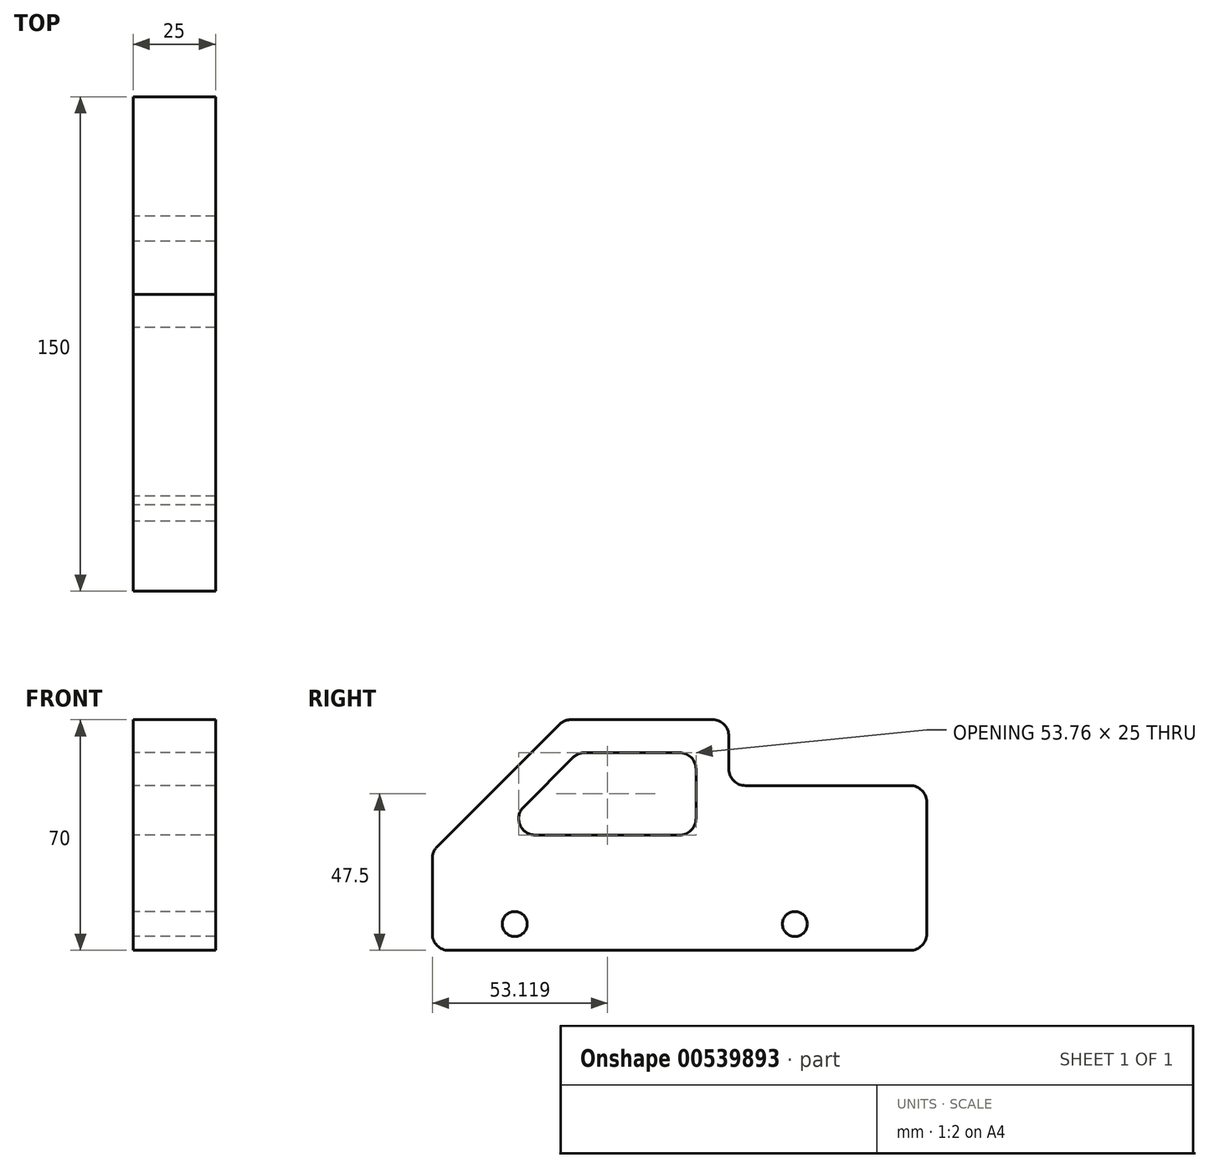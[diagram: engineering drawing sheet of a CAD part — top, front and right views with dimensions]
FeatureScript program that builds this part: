
annotation { "Feature Type Name" : "Feature", "Feature Type Description" : "" }
export const myFeature = defineFeature(function(context is Context, id is Id, definition is map)
    precondition{}
    {
        {
            var Q0;
            Q0=qCreatedBy(makeId("Right.planeOp"),FACE);
            var sketch = newSketch(context, id + "F0", { "sketchPlane" : qUnion([Q0])});
            skLineSegment(sketch, "E0", {"start": v(0, 0) * mm, "end": v(0, 30) * mm});
            skLineSegment(sketch, "E1", {"start": v(0, 30) * mm, "end": v(40, 70) * mm});
            skLineSegment(sketch, "E2", {"start": v(40, 70) * mm, "end": v(90, 70) * mm});
            skLineSegment(sketch, "E3", {"start": v(90, 70) * mm, "end": v(90, 50) * mm});
            skLineSegment(sketch, "E4", {"start": v(90, 50) * mm, "end": v(150, 50) * mm});
            skLineSegment(sketch, "E5", {"start": v(150, 50) * mm, "end": v(150, 0) * mm});
            skLineSegment(sketch, "E6", {"start": v(150, 0) * mm, "end": v(0, 0) * mm});
            skLineSegment(sketch, "E7.0", {"start": v(80, 60) * mm, "end": v(80, 35) * mm});
            skLineSegment(sketch, "E7.1", {"start": v(44.14, 60) * mm, "end": v(80, 60) * mm});
            skLineSegment(sketch, "E7.2", {"start": v(19.14, 35) * mm, "end": v(44.14, 60) * mm});
            skLineSegment(sketch, "E8", {"start": v(19.14, 35) * mm, "end": v(80, 35) * mm});
            skCircle(sketch, "E9", {"center": v(25, 8) * mm, "radius": 3.79 * mm});
            skCircle(sketch, "E10", {"center": v(110, 8) * mm, "radius": 3.79 * mm});
            skSolve(sketch);
        }
        {
            var Q0;
            Q0=makeQuery(id+"F0.imprint","IMPRINT",FACE,{"disambiguationData":[TD([[makeQuery(id+"F0.imprint","IMPRINT",EDGE,{"derivedFrom":sQuery(id+"F0.wireOp",EDGE,"E0")}),-1.0]])]});
            extrude(context, id + "F1", {"entities" : qUnion([Q0]), "depth" : 25 * mm, "offsetDistance" : 25 * mm});
        }
        {
            var Q0;
            Q0=makeQuery(id+"F1.opExtrude","SWEPT_EDGE",EDGE,{"disambiguationData":[OSD([sQuery(id+"F0.wireOp",EDGE,"E2"),sQuery(id+"F0.wireOp",EDGE,"E3")])]});
            var Q1;
            Q1=makeQuery(id+"F1.opExtrude","SWEPT_EDGE",EDGE,{"disambiguationData":[OSD([sQuery(id+"F0.wireOp",EDGE,"E3"),sQuery(id+"F0.wireOp",EDGE,"E4")])]});
            var Q2;
            Q2=makeQuery(id+"F1.opExtrude","SWEPT_EDGE",EDGE,{"disambiguationData":[OSD([sQuery(id+"F0.wireOp",EDGE,"E4"),sQuery(id+"F0.wireOp",EDGE,"E5")])]});
            var Q3;
            Q3=makeQuery(id+"F1.opExtrude","SWEPT_EDGE",EDGE,{"disambiguationData":[OSD([sQuery(id+"F0.wireOp",EDGE,"E5"),sQuery(id+"F0.wireOp",EDGE,"E6")])]});
            var Q4;
            Q4=makeQuery(id+"F1.opExtrude","SWEPT_EDGE",EDGE,{"disambiguationData":[OSD([sQuery(id+"F0.wireOp",EDGE,"E1"),sQuery(id+"F0.wireOp",EDGE,"E2")])]});
            var Q5;
            Q5=makeQuery(id+"F1.opExtrude","SWEPT_EDGE",EDGE,{"disambiguationData":[OSD([sQuery(id+"F0.wireOp",EDGE,"E0"),sQuery(id+"F0.wireOp",EDGE,"E1")])]});
            var Q6;
            Q6=makeQuery(id+"F1.opExtrude","SWEPT_EDGE",EDGE,{"disambiguationData":[OSD([sQuery(id+"F0.wireOp",EDGE,"E0"),sQuery(id+"F0.wireOp",EDGE,"E6")])]});
            fillet(context, id + "F2", {"entities" : qUnion([Q0, Q1, Q2, Q3, Q4, Q5, Q6]), "radius" : 5 * mm, "tangentPropagation" : true, "allowEdgeOverflow" : false});
        }
        {
            var Q0;
            Q0=makeQuery(id+"F1.opExtrude","SWEPT_EDGE",EDGE,{"disambiguationData":[OSD([sQuery(id+"F0.wireOp",EDGE,"E7.2"),sQuery(id+"F0.wireOp",EDGE,"E8")])]});
            var Q1;
            Q1=makeQuery(id+"F1.opExtrude","SWEPT_EDGE",EDGE,{"disambiguationData":[OSD([sQuery(id+"F0.wireOp",EDGE,"E7.0"),sQuery(id+"F0.wireOp",EDGE,"E7.1")])]});
            var Q2;
            Q2=makeQuery(id+"F1.opExtrude","SWEPT_EDGE",EDGE,{"disambiguationData":[OSD([sQuery(id+"F0.wireOp",EDGE,"E7.1"),sQuery(id+"F0.wireOp",EDGE,"E7.2")])]});
            var Q3;
            Q3=makeQuery(id+"F1.opExtrude","SWEPT_EDGE",EDGE,{"disambiguationData":[OSD([sQuery(id+"F0.wireOp",EDGE,"E7.0"),sQuery(id+"F0.wireOp",EDGE,"E8")])]});
            fillet(context, id + "F3", {"entities" : qUnion([Q0, Q1, Q2, Q3]), "radius" : 5 * mm, "tangentPropagation" : true, "allowEdgeOverflow" : false});
        }
    });
